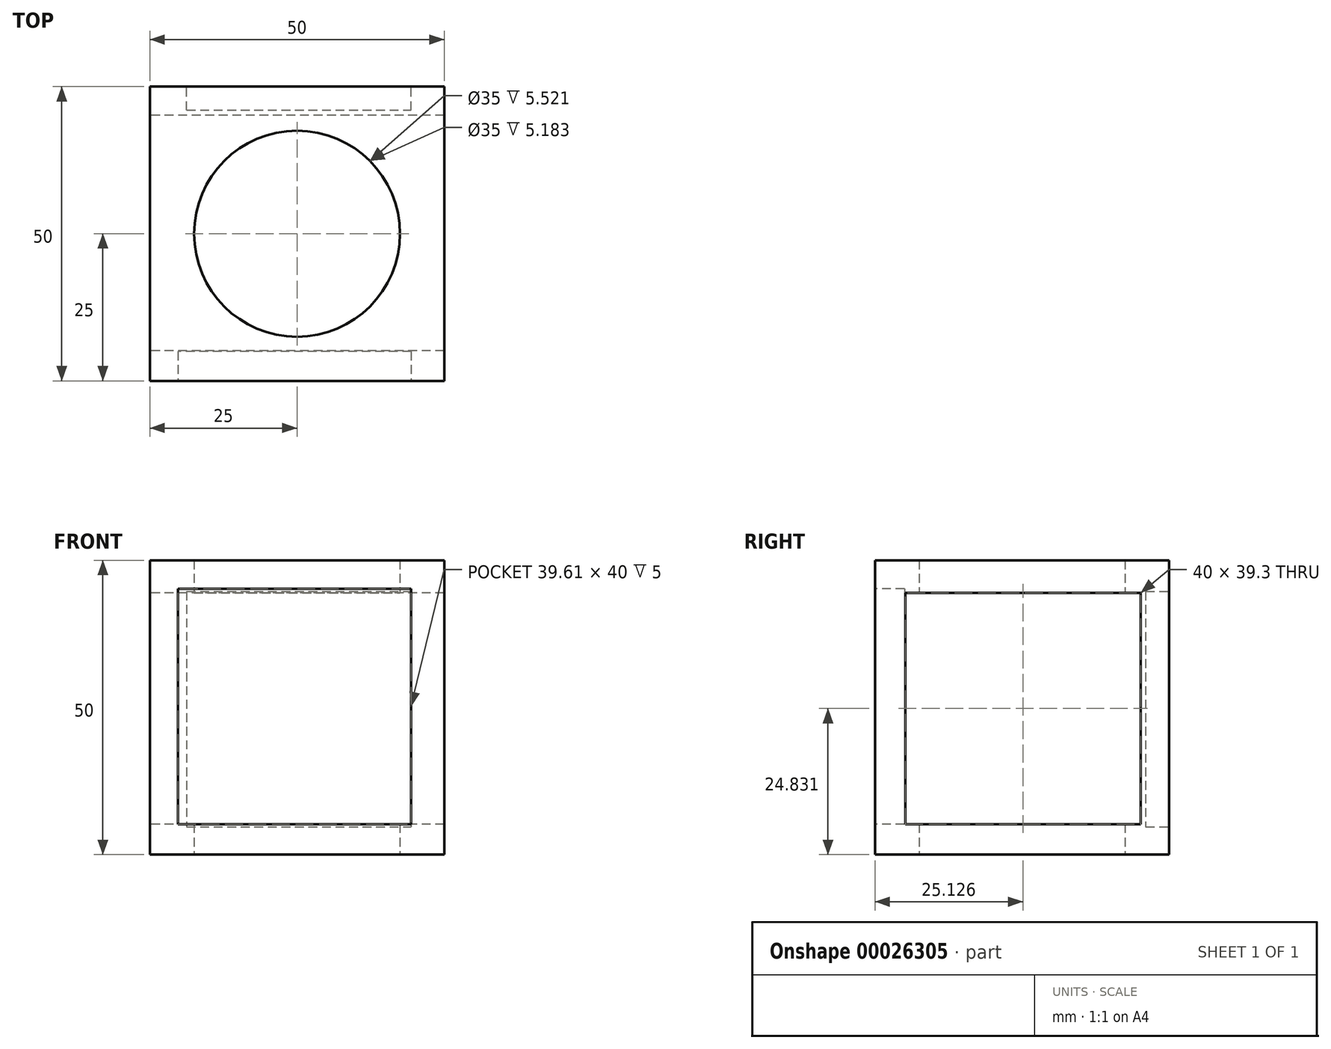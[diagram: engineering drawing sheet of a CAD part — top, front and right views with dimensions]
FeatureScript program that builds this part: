
annotation { "Feature Type Name" : "Feature", "Feature Type Description" : "" }
export const myFeature = defineFeature(function(context is Context, id is Id, definition is map)
    precondition{}
    {
        {
            var Q0;
            Q0=qCreatedBy(makeId("Top.planeOp"),FACE);
            var sketch = newSketch(context, id + "F0", { "sketchPlane" : qUnion([Q0])});
            skLineSegment(sketch, "E0.rect.bottom", {"start": v(-25, 25) * mm, "end": v(25, 25) * mm});
            skLineSegment(sketch, "E0.rect.top", {"start": v(-25, -25) * mm, "end": v(25, -25) * mm});
            skLineSegment(sketch, "E0.rect.left", {"start": v(-25, 25) * mm, "end": v(-25, -25) * mm});
            skLineSegment(sketch, "E0.rect.right", {"start": v(25, 25) * mm, "end": v(25, -25) * mm});
            skPoint(sketch, "E0.rect.middle", {"position": v(0, 0) * mm});
            skSolve(sketch);
        }
        {
            var Q0;
            Q0=makeQuery(id+"F0.imprint","IMPRINT",FACE,{"disambiguationData":[TD([[makeQuery(id+"F0.imprint","IMPRINT",EDGE,{"derivedFrom":sQuery(id+"F0.wireOp",EDGE,"E0.rect.bottom")}),-1.0]])]});
            extrude(context, id + "F1", {"entities" : qUnion([Q0]), "depth" : 50 * mm});
        }
        {
            var Q0;
            Q0=makeQuery(id+"F1.opExtrude","CAP_FACE",FACE,{"disambiguationData":[OSD([sQuery(id+"F0.wireOp",EDGE,"E0.rect.bottom"),sQuery(id+"F0.wireOp",EDGE,"E0.rect.top"),sQuery(id+"F0.wireOp",EDGE,"E0.rect.left"),sQuery(id+"F0.wireOp",EDGE,"E0.rect.right")])],"isStart":true});
            var sketch = newSketch(context, id + "F2", { "sketchPlane" : qUnion([Q0])});
            skCircle(sketch, "E1", {"center": v(0, 0) * mm, "radius": 17.5 * mm});
            skSolve(sketch);
        }
        {
            var Q0;
            Q0=makeQuery(id+"F2.imprint","IMPRINT",FACE,{"disambiguationData":[TD([[makeQuery(id+"F2.imprint","IMPRINT",EDGE,{"derivedFrom":sQuery(id+"F2.wireOp",EDGE,"E1")}),1.0]])]});
            extrude(context, id + "F3", {"entities" : qUnion([Q0]), "operationType" : NewBodyOperationType.REMOVE, "oppositeDirection" : true, "depth" : 50 * mm});
        }
        {
            var Q0;
            Q0=makeQuery(id+"F1.opExtrude","SWEPT_FACE",FACE,{"disambiguationData":[OSD([sQuery(id+"F0.wireOp",EDGE,"E0.rect.bottom")])]});
            var sketch = newSketch(context, id + "F4", { "sketchPlane" : qUnion([Q0])});
            skLineSegment(sketch, "E2.bottom", {"start": v(18.76, 44.71) * mm, "end": v(-19.4, 44.71) * mm});
            skLineSegment(sketch, "E2.top", {"start": v(18.76, 4.71) * mm, "end": v(-19.4, 4.71) * mm});
            skLineSegment(sketch, "E2.left", {"start": v(18.76, 44.71) * mm, "end": v(18.76, 4.71) * mm});
            skLineSegment(sketch, "E2.right", {"start": v(-19.4, 44.71) * mm, "end": v(-19.4, 4.71) * mm});
            skSolve(sketch);
        }
        {
            var Q0;
            Q0=makeQuery(id+"F4.imprint","IMPRINT",FACE,{"disambiguationData":[TD([[makeQuery(id+"F4.imprint","IMPRINT",EDGE,{"derivedFrom":sQuery(id+"F4.wireOp",EDGE,"E2.bottom")}),1.0]])]});
            extrude(context, id + "F5", {"entities" : qUnion([Q0]), "operationType" : NewBodyOperationType.REMOVE, "oppositeDirection" : true, "depth" : 4 * mm});
        }
        {
            var Q0;
            Q0=makeQuery(id+"F1.opExtrude","SWEPT_FACE",FACE,{"disambiguationData":[OSD([sQuery(id+"F0.wireOp",EDGE,"E0.rect.top")])]});
            var sketch = newSketch(context, id + "F6", { "sketchPlane" : qUnion([Q0])});
            skLineSegment(sketch, "E3.bottom", {"start": v(19.4, 45.15) * mm, "end": v(-20.22, 45.15) * mm});
            skLineSegment(sketch, "E3.top", {"start": v(19.4, 5.15) * mm, "end": v(-20.22, 5.15) * mm});
            skLineSegment(sketch, "E3.left", {"start": v(19.4, 45.15) * mm, "end": v(19.4, 5.15) * mm});
            skLineSegment(sketch, "E3.right", {"start": v(-20.22, 45.15) * mm, "end": v(-20.22, 5.15) * mm});
            skSolve(sketch);
        }
        {
            var Q0;
            Q0=makeQuery(id+"F6.imprint","IMPRINT",FACE,{"disambiguationData":[TD([[makeQuery(id+"F6.imprint","IMPRINT",EDGE,{"derivedFrom":sQuery(id+"F6.wireOp",EDGE,"E3.bottom")}),1.0]])]});
            extrude(context, id + "F7", {"entities" : qUnion([Q0]), "operationType" : NewBodyOperationType.REMOVE, "oppositeDirection" : true, "depth" : 5 * mm});
        }
        {
            var Q0;
            Q0=makeQuery(id+"F1.opExtrude","SWEPT_FACE",FACE,{"disambiguationData":[OSD([sQuery(id+"F0.wireOp",EDGE,"E0.rect.left")])]});
            var sketch = newSketch(context, id + "F8", { "sketchPlane" : qUnion([Q0])});
            skLineSegment(sketch, "E4.bottom", {"start": v(-20.13, 44.48) * mm, "end": v(19.87, 44.48) * mm});
            skLineSegment(sketch, "E4.top", {"start": v(-20.13, 5.18) * mm, "end": v(19.87, 5.18) * mm});
            skLineSegment(sketch, "E4.left", {"start": v(-20.13, 44.48) * mm, "end": v(-20.13, 5.18) * mm});
            skLineSegment(sketch, "E4.right", {"start": v(19.87, 44.48) * mm, "end": v(19.87, 5.18) * mm});
            skSolve(sketch);
        }
        {
            var Q0;
            Q0=makeQuery(id+"F8.imprint","IMPRINT",FACE,{"disambiguationData":[TD([[makeQuery(id+"F8.imprint","IMPRINT",EDGE,{"derivedFrom":sQuery(id+"F8.wireOp",EDGE,"E4.bottom")}),-1.0]])]});
            extrude(context, id + "F9", {"entities" : qUnion([Q0]), "operationType" : NewBodyOperationType.REMOVE, "oppositeDirection" : true, "depth" : 50 * mm});
        }
    });
